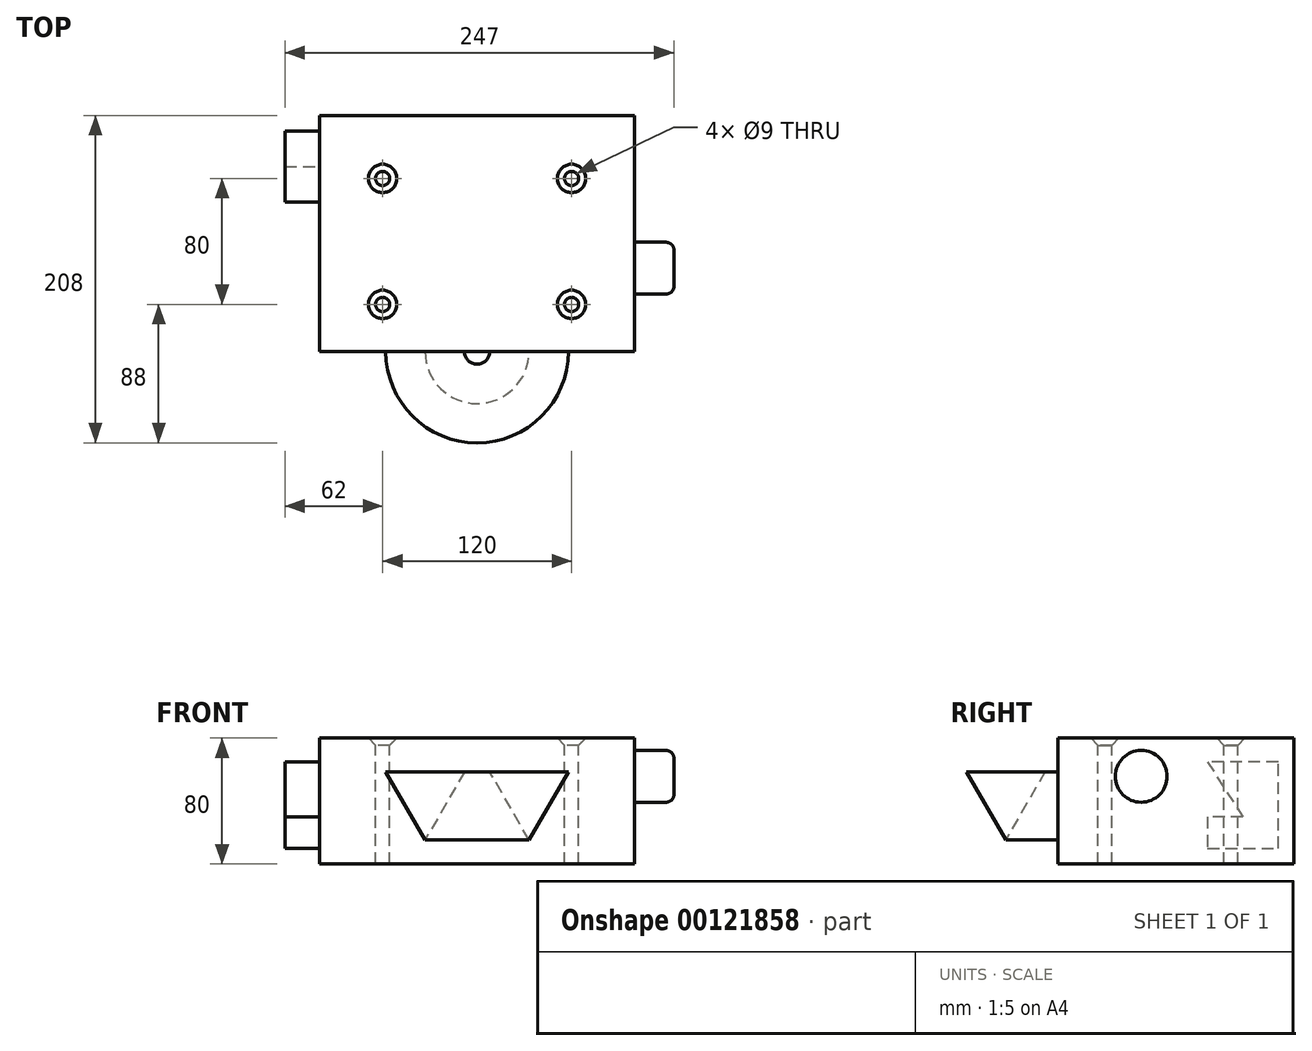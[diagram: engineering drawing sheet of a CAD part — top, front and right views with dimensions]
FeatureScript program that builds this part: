
annotation { "Feature Type Name" : "Feature", "Feature Type Description" : "" }
export const myFeature = defineFeature(function(context is Context, id is Id, definition is map)
    precondition{}
    {
        {
            var Q0;
            Q0=qCreatedBy(makeId("Top.planeOp"),FACE);
            var sketch = newSketch(context, id + "F0", { "sketchPlane" : qUnion([Q0])});
            skLineSegment(sketch, "E0.bottom", {"start": v(100, 75) * mm, "end": v(-100, 75) * mm});
            skLineSegment(sketch, "E0.top", {"start": v(100, -75) * mm, "end": v(-100, -75) * mm});
            skLineSegment(sketch, "E0.left", {"start": v(100, 75) * mm, "end": v(100, -75) * mm});
            skLineSegment(sketch, "E0.right", {"start": v(-100, 75) * mm, "end": v(-100, -75) * mm});
            skPoint(sketch, "E0.middle", {"position": v(0, 0) * mm});
            skSolve(sketch);
        }
        {
            var Q0;
            Q0 = qSketchRegion(id + "F0", true);
            extrude(context, id + "F1", {"entities" : qUnion([Q0]), "depth" : 80 * mm});
        }
        {
            var Q0;
            Q0=makeQuery(id+"F1.opExtrude","CAP_FACE",FACE,{"disambiguationData":[OSD([sQuery(id+"F0.wireOp",EDGE,"E0.bottom"),sQuery(id+"F0.wireOp",EDGE,"E0.top"),sQuery(id+"F0.wireOp",EDGE,"E0.left"),sQuery(id+"F0.wireOp",EDGE,"E0.right")])],"isStart":false});
            var sketch = newSketch(context, id + "F12", { "sketchPlane" : qUnion([Q0])});
            skPoint(sketch, "E1", {"position": v(-60, 35) * mm});
            skLineSegment(sketch, "E2", {"start": v(58.7, 93.73) * mm, "end": v(58.7, 93.73) * mm});
            skLineSegment(sketch, "E3", {"start": v(-60, 35) * mm, "end": v(60, 35) * mm});
            skLineSegment(sketch, "E4", {"start": v(60, 35) * mm, "end": v(60, -45) * mm});
            skLineSegment(sketch, "E5", {"start": v(60, -45) * mm, "end": v(-60, -45) * mm});
            skLineSegment(sketch, "E6", {"start": v(-60, -45) * mm, "end": v(-60, 35) * mm});
            skSolve(sketch);
        }
        {
            var Q0;
            Q0=sQuery(id+"F12.wireOp",VERTEX,"E1");
            var Q1;
            Q1=sQuery(id+"F12.wireOp",VERTEX,"E5.end");
            var Q2;
            Q2=sQuery(id+"F12.wireOp",VERTEX,"E4.start");
            var Q3;
            Q3=sQuery(id+"F12.wireOp",VERTEX,"E5.start");
            var Q4;
            Q4=makeQuery(id+"F1.opExtrude","SWEPT_BODY",BODY,{"disambiguationData":[OSD([sQuery(id+"F0.wireOp",EDGE,"E0.bottom"),sQuery(id+"F0.wireOp",EDGE,"E0.top"),sQuery(id+"F0.wireOp",EDGE,"E0.left"),sQuery(id+"F0.wireOp",EDGE,"E0.right")])]});
            hole(context, id + "F13", {"style" : HoleStyle.C_SINK, "endStyle" : HoleEndStyle.THROUGH, "holeDiameter" : 9 * mm, "cSinkDiameter" : 18 * mm, "cSinkAngle" : 90 * degree, "locations" : qUnion([Q0, Q1, Q2, Q3]), "scope" : qUnion([Q4]), "isTappedThrough" : true});
        }
        {
            var Q0;
            Q0=makeQuery(id+"F1.opExtrude","SWEPT_FACE",FACE,{"disambiguationData":[OSD([sQuery(id+"F0.wireOp",EDGE,"E0.left")])]});
            var sketch = newSketch(context, id + "F2", { "sketchPlane" : qUnion([Q0])});
            skLineSegment(sketch, "E7", {"start": v(17.46, 50.54) * mm, "end": v(57.46, 50.54) * mm});
            skLineSegment(sketch, "E8", {"start": v(57.46, 50.54) * mm, "end": v(57.46, 20.54) * mm});
            skLineSegment(sketch, "E9", {"start": v(57.46, 20.54) * mm, "end": v(17.46, 20.54) * mm});
            skLineSegment(sketch, "E10", {"start": v(17.46, 20.54) * mm, "end": v(17.46, 50.54) * mm});
            skCircle(sketch, "E11", {"center": v(-22, 55.7) * mm, "radius": 16.46 * mm});
            skCircle(sketch, "E12.0.1.0", {"center": v(-22, 95.7) * mm, "radius": 16.46 * mm});
            skCircle(sketch, "E12.1.0.0", {"center": v(28, 55.7) * mm, "radius": 16.46 * mm});
            skCircle(sketch, "E12.1.1.0", {"center": v(28, 95.7) * mm, "radius": 16.46 * mm});
            skCircle(sketch, "E12.2.0.0", {"center": v(78, 55.7) * mm, "radius": 16.46 * mm});
            skCircle(sketch, "E12.2.1.0", {"center": v(78, 95.7) * mm, "radius": 16.46 * mm});
            skLineSegment(sketch, "E12.direction1", {"start": v(-22, 55.7) * mm, "end": v(28, 55.7) * mm, "construction": true});
            skLineSegment(sketch, "E12.direction2", {"start": v(-22, 55.7) * mm, "end": v(-22, 95.7) * mm, "construction": true});
            skCircle(sketch, "E13.0.0.2", {"center": v(-22, 135.7) * mm, "radius": 16.46 * mm});
            skCircle(sketch, "E13.0.1.2", {"center": v(28, 135.7) * mm, "radius": 16.46 * mm});
            skCircle(sketch, "E13.0.2.2", {"center": v(78, 135.7) * mm, "radius": 16.46 * mm});
            skSolve(sketch);
        }
        {
            var Q0;
            Q0=makeQuery(id+"F2.imprint","IMPRINT",FACE,{"disambiguationData":[TD([[makeQuery(id+"F2.imprint","IMPRINT",EDGE,{"derivedFrom":sQuery(id+"F2.wireOp",EDGE,"E13.0.2.2")}),1.0]])]});
            var Q1;
            Q1=sQuery(id+"F2.wireOp",EDGE,"E13.0.2.2");
            extrude(context, id + "F3", {"entities" : qUnion([Q0]), "surfaceEntities" : qUnion([Q1]), "depth" : 60 * mm});
        }
        {
            var Q0;
            Q0=makeQuery(id+"F2.imprint","IMPRINT",FACE,{"disambiguationData":[TD([[makeQuery(id+"F2.imprint","IMPRINT",EDGE,{"derivedFrom":sQuery(id+"F2.wireOp",EDGE,"E11")}),1.0]])]});
            var Q1;
            Q1=sQuery(id+"F2.wireOp",EDGE,"E11");
            extrude(context, id + "F4", {"entities" : qUnion([Q0]), "operationType" : NewBodyOperationType.ADD, "surfaceEntities" : qUnion([Q1]), "depth" : 25 * mm});
        }
        {
            var Q0;
            Q0=makeQuery(id+"F4.opExtrude","CAP_EDGE",EDGE,{"disambiguationData":[OSD([sQuery(id+"F2.wireOp",EDGE,"E11")])],"isStart":true});
            var Q1;
            Q1=makeQuery(id+"F4.opExtrude","CAP_EDGE",EDGE,{"disambiguationData":[OSD([sQuery(id+"F2.wireOp",EDGE,"E11")])],"isStart":false});
            fillet(context, id + "F14", {"entities" : qUnion([Q0, Q1]), "radius" : 5 * mm, "tangentPropagation" : true, "allowEdgeOverflow" : false});
        }
        {
            var Q0;
            Q0=makeQuery(id+"F3.opExtrude","CAP_EDGE",EDGE,{"disambiguationData":[OSD([sQuery(id+"F2.wireOp",EDGE,"E13.0.2.2")])],"isStart":false});
            var Q1;
            Q1=makeQuery(id+"F3.opExtrude","CAP_EDGE",EDGE,{"disambiguationData":[OSD([sQuery(id+"F2.wireOp",EDGE,"E13.0.2.2")])],"isStart":true});
            fillet(context, id + "F5", {"entities" : qUnion([Q0, Q1]), "radius" : 5 * mm, "tangentPropagation" : true, "allowEdgeOverflow" : false});
        }
        {
            var Q0;
            Q0=makeQuery(id+"F3.opExtrude","SWEPT_BODY",BODY,{"disambiguationData":[OSD([sQuery(id+"F2.wireOp",EDGE,"E13.0.2.2")])]});
            var Q1;
            Q1=qCreatedBy(makeId("Right.planeOp"),FACE);
            mirror(context, id + "F6", {"entities" : qUnion([Q0]), "mirrorPlane" : qUnion([Q1])});
        }
        {
            var Q0;
            Q0=makeQuery(id+"F1.opExtrude","SWEPT_FACE",FACE,{"disambiguationData":[OSD([sQuery(id+"F0.wireOp",EDGE,"E0.top")])]});
            var sketch = newSketch(context, id + "F7", { "sketchPlane" : qUnion([Q0])});
            skLineSegment(sketch, "E14", {"start": v(-58, 58.63) * mm, "end": v(-8, 58.63) * mm});
            skLineSegment(sketch, "E15", {"start": v(-8, 58.63) * mm, "end": v(-33, 15.33) * mm});
            skPoint(sketch, "E15.endSnap0", {"position": v(-33, 58.63) * mm});
            skLineSegment(sketch, "E16", {"start": v(-33, 15.33) * mm, "end": v(-58, 58.63) * mm});
            skLineSegment(sketch, "E17", {"start": v(0, 80) * mm, "end": v(0, 0) * mm, "construction": true});
            skLineSegment(sketch, "E18.MirrorCS", {"start": v(33, 15.33) * mm, "end": v(58, 58.63) * mm});
            skLineSegment(sketch, "E19.MirrorCS", {"start": v(8, 58.63) * mm, "end": v(33, 15.33) * mm});
            skLineSegment(sketch, "E20.MirrorCS", {"start": v(58, 58.63) * mm, "end": v(8, 58.63) * mm});
            skSolve(sketch);
        }
        {
            var Q0;
            Q0=makeQuery(id+"F7.imprint","IMPRINT",FACE,{"disambiguationData":[TD([[makeQuery(id+"F7.imprint","IMPRINT",EDGE,{"derivedFrom":sQuery(id+"F7.wireOp",EDGE,"E18.MirrorCS")}),1.0]])]});
            var Q1;
            Q1=sQuery(id+"F7.wireOp",EDGE,"E17");
            revolve(context, id + "F15", {"operationType" : NewBodyOperationType.ADD, "entities" : qUnion([Q0]), "axis" : qUnion([Q1]), "revolveType" : RevolveType.FULL});
        }
        {
            var Q0;
            Q0=makeQuery(id+"F6.opPattern","COPY",BODY,{"derivedFrom":makeQuery(id+"F3.opExtrude","SWEPT_BODY",BODY,{"disambiguationData":[OSD([sQuery(id+"F2.wireOp",EDGE,"E13.0.2.2")])]}),"instanceName":"1"});
            deleteBodies(context, id + "F8", {"entities" : qUnion([Q0])});
        }
        {
            var Q0;
            Q0=makeQuery(id+"F3.opExtrude","SWEPT_BODY",BODY,{"disambiguationData":[OSD([sQuery(id+"F2.wireOp",EDGE,"E13.0.2.2")])]});
            deleteBodies(context, id + "F9", {"entities" : qUnion([Q0])});
        }
        {
            var Q0;
            Q0=makeQuery(id+"F1.opExtrude","SWEPT_FACE",FACE,{"disambiguationData":[OSD([sQuery(id+"F0.wireOp",EDGE,"E0.right")])]});
            var sketch = newSketch(context, id + "F10", { "sketchPlane" : qUnion([Q0])});
            skLineSegment(sketch, "E21", {"start": v(-65, 65) * mm, "end": v(-20, 65) * mm});
            skLineSegment(sketch, "E22", {"start": v(-20, 65) * mm, "end": v(-42.5, 30) * mm});
            skPoint(sketch, "E22.endSnap0", {"position": v(-42.5, 65) * mm});
            skLineSegment(sketch, "E23", {"start": v(-42.5, 30) * mm, "end": v(-20, 30) * mm});
            skLineSegment(sketch, "E24", {"start": v(-20, 30) * mm, "end": v(-20, 10) * mm});
            skLineSegment(sketch, "E25", {"start": v(-20, 10) * mm, "end": v(-65, 10) * mm});
            skLineSegment(sketch, "E26", {"start": v(-65, 10) * mm, "end": v(-65, 65) * mm});
            skSolve(sketch);
        }
        {
            var Q0;
            Q0 = qSketchRegion(id + "F10", true);
            extrude(context, id + "F11", {"entities" : qUnion([Q0]), "operationType" : NewBodyOperationType.ADD, "depth" : 22 * mm});
        }
    });
